# Revit family: Floor_mount_three_compartment_dependabilt_sink-Elkay-3C10X14-0X (1)
name_source: partatom
category: Plumbing Fixtures
units: mm (PartAtom-declared; Revit-internal decimal feet)

## family parameters
Always vertical = Yes
Cut with Voids When Loaded = No
Maintain Annotation Orientation = No
OmniClass Number = 23.45.05.14.14
OmniClass Title = Sinks/Lavatories
Part Type = Normal
Room Calculation Point = No
Round Connector Dimension = Use Diameter
Shared = No
Work Plane-Based = No

## types (1)
- 3C10X14-0X (Floor Mount Three Compartment Dependabilt Sink)
    Approx. Shipping Weight (lbs) = 102
    Assembly Code = D2010400
    Backsplash Height = 9.750"
    Bowl 1 Dimensions = 10 inch x 14 inch x 10 inch
    Bowl 2 Dimensions = 10 inch x 14 inch x 10 inch
    Bowl 3 Dimensions = 10 inch x 14 inch x 10 inch
    Bowl Depth = 10.000"
    Bowl Length = 10.000"
    Bowl Prof. dist. = 7.000"
    Bowl Width = 14.000"
    Bowl filler length = 6.000"
    Bowl filler width = 10.000"
    Circ Prof dist = 10.407"
    Circ Rim start plane = 8.907"
    Circ rim end plane = 19.313"
    Default Elevation = 0.000"
    Description = Dependabilt™ Stainless Steel 39 inch x 19 13/16 inch x 43 3/4 inch 16 Gauge Three Compartment Sink with Stainless Steel Legs
    Dist btw bowls = 2.000"
    Drain Location = Center
    Drain Size = 3.500"
    Drainboard Location = No Drain Board
    Faucet Hole 1 Loc. = 15.500"
    Installation Type = Floor Mount
    Legs Distance Y = 10.000"
    Legs distance X = 29.500"
    Main Material = Finish-Elkay-Stainless Steel
    Manufacturer = Elkay Manufacturer Company
    Manufacturer Brand = Elkay (by Zurn Elkay Water Solutions)
    Model = 3C10X14-0X
    No. of Bowls = 3
    Outlet Connection Size (inch) = 1.500"
    Product Documentation Link = https://www.elkayfiles.com
    Product Page URL = https://www.elkay.com
    Product Weight (lbs) = 102
    Product data URL = https://bimobject.com
    Rim Profile Dist = 19.500"
    Rim Width = 17.813"
    Sink Depth = 43.750"
    Sink Dimensions = 39 inch x 19 13/16 inch x 43 3/4 inch
    Sink Length = 39.000"
    Sink Width = 19.813"
    URL = https://www.elkay.com

## geometry (parser evidence)
native form markers: Sweep x3
no freeform markers — native parametric forms only
